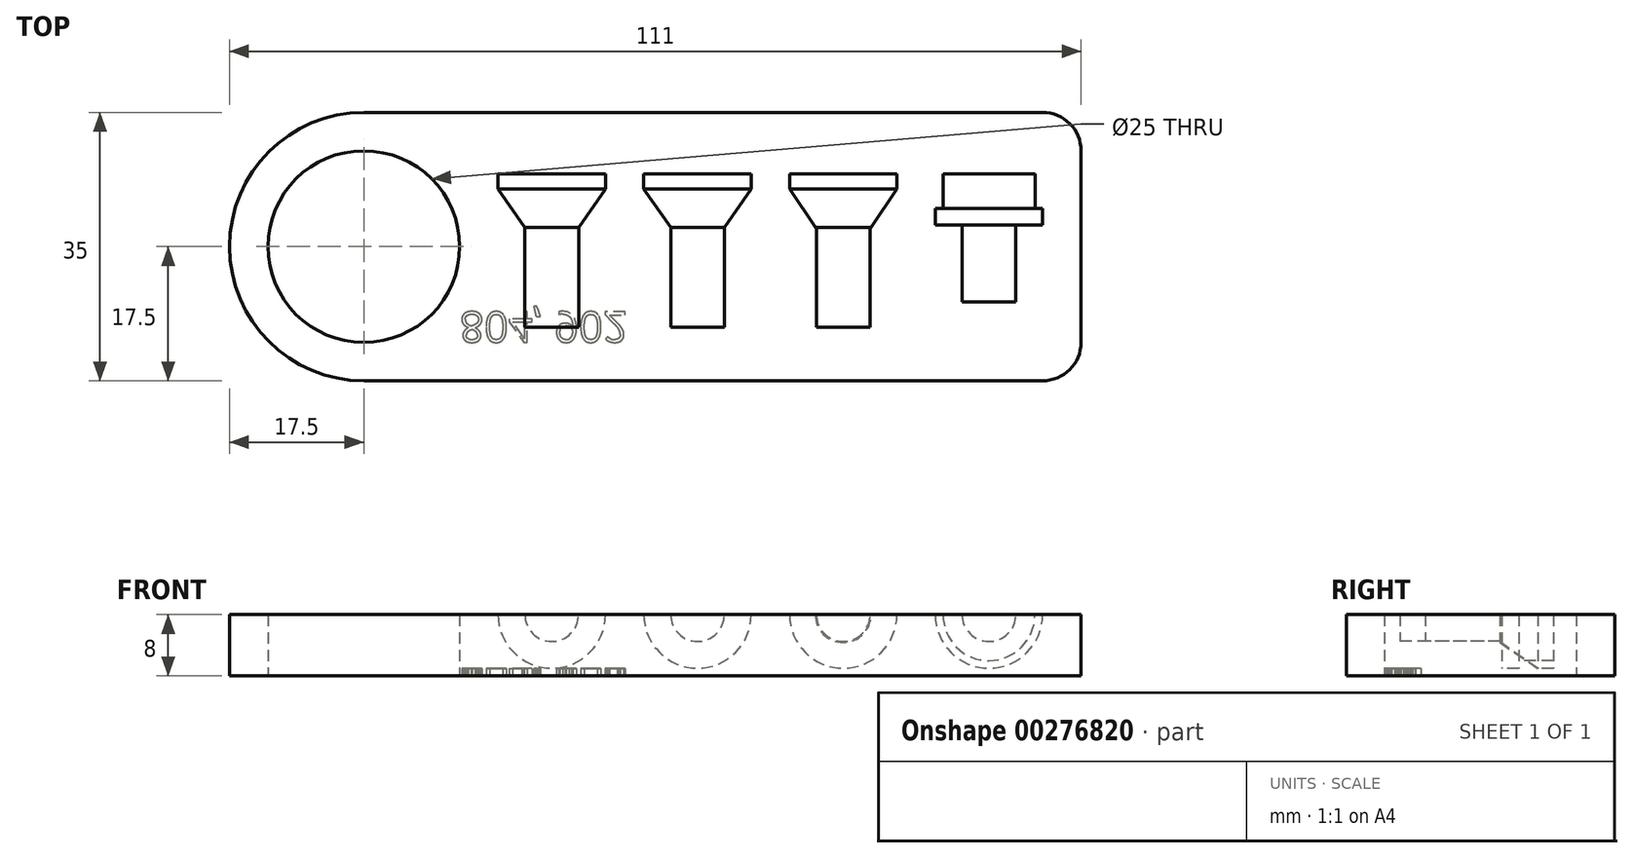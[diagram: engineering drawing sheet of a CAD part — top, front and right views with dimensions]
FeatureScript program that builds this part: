
annotation { "Feature Type Name" : "Feature", "Feature Type Description" : "" }
export const myFeature = defineFeature(function(context is Context, id is Id, definition is map)
    precondition{}
    {
        {
            var Q0;
            Q0=qCreatedBy(makeId("Top.planeOp"),FACE);
            var sketch = newSketch(context, id + "F0", { "sketchPlane" : qUnion([Q0])});
            skLineSegment(sketch, "E0.bottom", {"start": v(17.5, 0) * mm, "end": v(106, 0) * mm});
            skLineSegment(sketch, "E0.top", {"start": v(17.5, 35) * mm, "end": v(106, 35) * mm});
            skLineSegment(sketch, "E0.left", {"start": v(0, 17.5) * mm, "end": v(0, 17.5) * mm});
            skLineSegment(sketch, "E0.right", {"start": v(111, 5) * mm, "end": v(111, 30) * mm});
            skLineSegment(sketch, "E1.bottom", {"start": v(0, 0) * mm, "end": v(17.5, 0) * mm, "construction": true});
            skLineSegment(sketch, "E1.top", {"start": v(0, 17.5) * mm, "end": v(17.5, 17.5) * mm, "construction": true});
            skLineSegment(sketch, "E1.left", {"start": v(0, 0) * mm, "end": v(0, 17.5) * mm, "construction": true});
            skLineSegment(sketch, "E1.right", {"start": v(17.5, 0) * mm, "end": v(17.5, 17.5) * mm, "construction": true});
            skCircle(sketch, "E2", {"center": v(17.5, 17.5) * mm, "radius": 12.5 * mm});
            skPoint(sketch, "E3.visualSharp", {"position": v(0, 0) * mm});
            skArc(sketch, "E3.filletArc", {"start": v(0, 17.5) * mm, "mid": v(5.13, 5.13) * mm, "end": v(17.5, 0) * mm});
            skPoint(sketch, "E4.visualSharp", {"position": v(0, 35) * mm});
            skArc(sketch, "E4.filletArc", {"start": v(17.5, 35) * mm, "mid": v(5.13, 29.87) * mm, "end": v(0, 17.5) * mm});
            skPoint(sketch, "E5.visualSharp", {"position": v(111, 35) * mm});
            skArc(sketch, "E5.filletArc", {"start": v(111, 30) * mm, "mid": v(109.54, 33.54) * mm, "end": v(106, 35) * mm});
            skPoint(sketch, "E6.visualSharp", {"position": v(111, 0) * mm});
            skArc(sketch, "E6.filletArc", {"start": v(106, 0) * mm, "mid": v(109.54, 1.46) * mm, "end": v(111, 5) * mm});
            skSolve(sketch);
        }
        {
            var Q0;
            Q0=makeQuery(id+"F0.imprint","IMPRINT",FACE,{"disambiguationData":[TD([[makeQuery(id+"F0.imprint","IMPRINT",EDGE,{"derivedFrom":sQuery(id+"F0.wireOp",EDGE,"E0.bottom")}),1.0]])]});
            extrude(context, id + "F1", {"entities" : qUnion([Q0]), "depth" : 8 * mm});
        }
        {
            var Q0;
            Q0=makeQuery(id+"F1.opExtrude","CAP_FACE",FACE,{"disambiguationData":[OSD([sQuery(id+"F0.wireOp",EDGE,"E0.bottom"),sQuery(id+"F0.wireOp",EDGE,"E0.top"),sQuery(id+"F0.wireOp",EDGE,"E0.right"),sQuery(id+"F0.wireOp",EDGE,"E2"),sQuery(id+"F0.wireOp",EDGE,"E3.filletArc"),sQuery(id+"F0.wireOp",EDGE,"E4.filletArc"),sQuery(id+"F0.wireOp",EDGE,"E5.filletArc"),sQuery(id+"F0.wireOp",EDGE,"E6.filletArc")])],"isStart":false});
            var sketch = newSketch(context, id + "F2", { "sketchPlane" : qUnion([Q0])});
            skLineSegment(sketch, "E7.bottom", {"start": v(0, 0) * mm, "end": v(42, 0) * mm, "construction": true});
            skLineSegment(sketch, "E7.top", {"start": v(0, 27) * mm, "end": v(42, 27) * mm, "construction": true});
            skLineSegment(sketch, "E7.left", {"start": v(0, 0) * mm, "end": v(0, 27) * mm, "construction": true});
            skLineSegment(sketch, "E7.right", {"start": v(42, 0) * mm, "end": v(42, 27) * mm, "construction": true});
            skLineSegment(sketch, "E8.bottom", {"start": v(42, 27) * mm, "end": v(49, 27) * mm});
            skLineSegment(sketch, "E8.left", {"start": v(42, 27) * mm, "end": v(42, 25) * mm});
            skLineSegment(sketch, "E8.right", {"start": v(49, 27) * mm, "end": v(49, 25) * mm});
            skLineSegment(sketch, "E9", {"start": v(42, 27) * mm, "end": v(61, 27) * mm, "construction": true});
            skLineSegment(sketch, "E10", {"start": v(61, 27) * mm, "end": v(80, 27) * mm, "construction": true});
            skLineSegment(sketch, "E11.bottom", {"start": v(61, 27) * mm, "end": v(68, 27) * mm});
            skLineSegment(sketch, "E11.left", {"start": v(61, 27) * mm, "end": v(61, 25) * mm});
            skLineSegment(sketch, "E11.right", {"start": v(68, 27) * mm, "end": v(68, 25) * mm});
            skLineSegment(sketch, "E12.bottom", {"start": v(80, 27) * mm, "end": v(87, 27) * mm});
            skLineSegment(sketch, "E12.left", {"start": v(80, 27) * mm, "end": v(80, 25) * mm});
            skLineSegment(sketch, "E12.right", {"start": v(87, 27) * mm, "end": v(87, 25) * mm});
            skLineSegment(sketch, "E13.left", {"start": v(42, 25) * mm, "end": v(42, 20) * mm});
            skLineSegment(sketch, "E14.left", {"start": v(61, 25) * mm, "end": v(61, 20) * mm});
            skLineSegment(sketch, "E15.top", {"start": v(83.5, 20) * mm, "end": v(83.63, 20) * mm});
            skLineSegment(sketch, "E15.left", {"start": v(80, 25) * mm, "end": v(80, 20) * mm});
            skLineSegment(sketch, "E16.top", {"start": v(80, 7) * mm, "end": v(83.5, 7) * mm});
            skLineSegment(sketch, "E16.left", {"start": v(80, 20) * mm, "end": v(80, 7) * mm});
            skLineSegment(sketch, "E16.right", {"start": v(83.5, 20) * mm, "end": v(83.5, 7) * mm});
            skLineSegment(sketch, "E17.top", {"start": v(61, 7) * mm, "end": v(64.5, 7) * mm});
            skLineSegment(sketch, "E17.left", {"start": v(61, 20) * mm, "end": v(61, 7) * mm});
            skLineSegment(sketch, "E17.right", {"start": v(64.5, 20) * mm, "end": v(64.5, 7) * mm});
            skLineSegment(sketch, "E18.top", {"start": v(42, 7) * mm, "end": v(45.5, 7) * mm});
            skLineSegment(sketch, "E18.left", {"start": v(42, 20) * mm, "end": v(42, 7) * mm});
            skLineSegment(sketch, "E18.right", {"start": v(45.5, 20) * mm, "end": v(45.5, 7) * mm});
            skLineSegment(sketch, "E19", {"start": v(49, 25) * mm, "end": v(45.5, 20) * mm});
            skLineSegment(sketch, "E20", {"start": v(68, 25) * mm, "end": v(64.5, 20) * mm});
            skLineSegment(sketch, "E21", {"start": v(87, 25) * mm, "end": v(83.63, 20) * mm});
            skLineSegment(sketch, "E22", {"start": v(80, 27) * mm, "end": v(99, 27) * mm, "construction": true});
            skLineSegment(sketch, "E23.bottom", {"start": v(99, 27) * mm, "end": v(105, 27) * mm});
            skLineSegment(sketch, "E23.left", {"start": v(99, 27) * mm, "end": v(99, 22.5) * mm});
            skLineSegment(sketch, "E23.right", {"start": v(105, 27) * mm, "end": v(105, 22.5) * mm});
            skLineSegment(sketch, "E24.bottom", {"start": v(105, 22.5) * mm, "end": v(106, 22.5) * mm});
            skLineSegment(sketch, "E24.top", {"start": v(102.5, 20.3) * mm, "end": v(106, 20.3) * mm});
            skLineSegment(sketch, "E24.left", {"start": v(99, 22.5) * mm, "end": v(99, 20.3) * mm});
            skLineSegment(sketch, "E24.right", {"start": v(106, 22.5) * mm, "end": v(106, 20.3) * mm});
            skLineSegment(sketch, "E25.top", {"start": v(99, 10.3) * mm, "end": v(102.5, 10.3) * mm});
            skLineSegment(sketch, "E25.left", {"start": v(99, 20.3) * mm, "end": v(99, 10.3) * mm});
            skLineSegment(sketch, "E25.right", {"start": v(102.5, 20.3) * mm, "end": v(102.5, 10.3) * mm});
            skSolve(sketch);
        }
        {
            var Q0;
            Q0=makeQuery(id+"F2.imprint","IMPRINT",FACE,{"disambiguationData":[TD([[makeQuery(id+"F2.imprint","IMPRINT",EDGE,{"derivedFrom":sQuery(id+"F2.wireOp",EDGE,"E23.bottom")}),-1.0]])]});
            var Q1;
            Q1=sQuery(id+"F2.wireOp",EDGE,"E25.left");
            revolve(context, id + "F3", {"operationType" : NewBodyOperationType.REMOVE, "entities" : qUnion([Q0]), "axis" : qUnion([Q1]), "revolveType" : RevolveType.FULL, "oppositeDirection" : true});
        }
        {
            var Q0;
            Q0=makeQuery(id+"F2.imprint","IMPRINT",FACE,{"disambiguationData":[TD([[makeQuery(id+"F2.imprint","IMPRINT",EDGE,{"derivedFrom":sQuery(id+"F2.wireOp",EDGE,"E12.bottom")}),-1.0]])]});
            var Q1;
            Q1=sQuery(id+"F2.wireOp",EDGE,"E16.left");
            revolve(context, id + "F4", {"operationType" : NewBodyOperationType.REMOVE, "entities" : qUnion([Q0]), "axis" : qUnion([Q1]), "revolveType" : RevolveType.FULL, "oppositeDirection" : true});
        }
        {
            var Q0;
            Q0=makeQuery(id+"F2.imprint","IMPRINT",FACE,{"disambiguationData":[TD([[makeQuery(id+"F2.imprint","IMPRINT",EDGE,{"derivedFrom":sQuery(id+"F2.wireOp",EDGE,"E11.bottom")}),-1.0]])]});
            var Q1;
            Q1=sQuery(id+"F2.wireOp",EDGE,"E17.left");
            revolve(context, id + "F5", {"operationType" : NewBodyOperationType.REMOVE, "entities" : qUnion([Q0]), "axis" : qUnion([Q1]), "revolveType" : RevolveType.FULL, "oppositeDirection" : true});
        }
        {
            var Q0;
            Q0=makeQuery(id+"F2.imprint","IMPRINT",FACE,{"disambiguationData":[TD([[makeQuery(id+"F2.imprint","IMPRINT",EDGE,{"derivedFrom":sQuery(id+"F2.wireOp",EDGE,"E8.bottom")}),-1.0]])]});
            var Q1;
            Q1=sQuery(id+"F2.wireOp",EDGE,"E18.left");
            revolve(context, id + "F6", {"operationType" : NewBodyOperationType.REMOVE, "entities" : qUnion([Q0]), "axis" : qUnion([Q1]), "revolveType" : RevolveType.FULL, "oppositeDirection" : true});
        }
        {
            var Q0;
            Q0=makeQuery(id+"F1.opExtrude","CAP_FACE",FACE,{"disambiguationData":[OSD([sQuery(id+"F0.wireOp",EDGE,"E0.bottom"),sQuery(id+"F0.wireOp",EDGE,"E0.top"),sQuery(id+"F0.wireOp",EDGE,"E0.right"),sQuery(id+"F0.wireOp",EDGE,"E2"),sQuery(id+"F0.wireOp",EDGE,"E3.filletArc"),sQuery(id+"F0.wireOp",EDGE,"E4.filletArc"),sQuery(id+"F0.wireOp",EDGE,"E5.filletArc"),sQuery(id+"F0.wireOp",EDGE,"E6.filletArc")])],"isStart":true});
            var sketch = newSketch(context, id + "F7", { "sketchPlane" : qUnion([Q0])});
            skLineSegment(sketch, "E26.bottom", {"start": v(0, 0) * mm, "end": v(30, 0) * mm, "construction": true});
            skLineSegment(sketch, "E26.top", {"start": v(0, -5) * mm, "end": v(30, -5) * mm, "construction": true});
            skLineSegment(sketch, "E26.left", {"start": v(0, 0) * mm, "end": v(0, -5) * mm, "construction": true});
            skLineSegment(sketch, "E26.right", {"start": v(30, 0) * mm, "end": v(30, -5) * mm, "construction": true});
            skText(sketch, "E27", { "text": "804, 902\n", "fontName": "OpenSans-Regular.ttf"});
            const initialGuessF7  = {"E27": [0.03, -0.009, 1, 0, 0.004]};
            skSetInitialGuess(sketch, initialGuessF7);
            skSolve(sketch);
        }
        {
            var Q0;
            Q0 = qSketchRegion(id + "F7", true);
            extrude(context, id + "F8", {"entities" : qUnion([Q0]), "operationType" : NewBodyOperationType.REMOVE, "oppositeDirection" : true, "depth" : 1 * mm});
        }
    });
